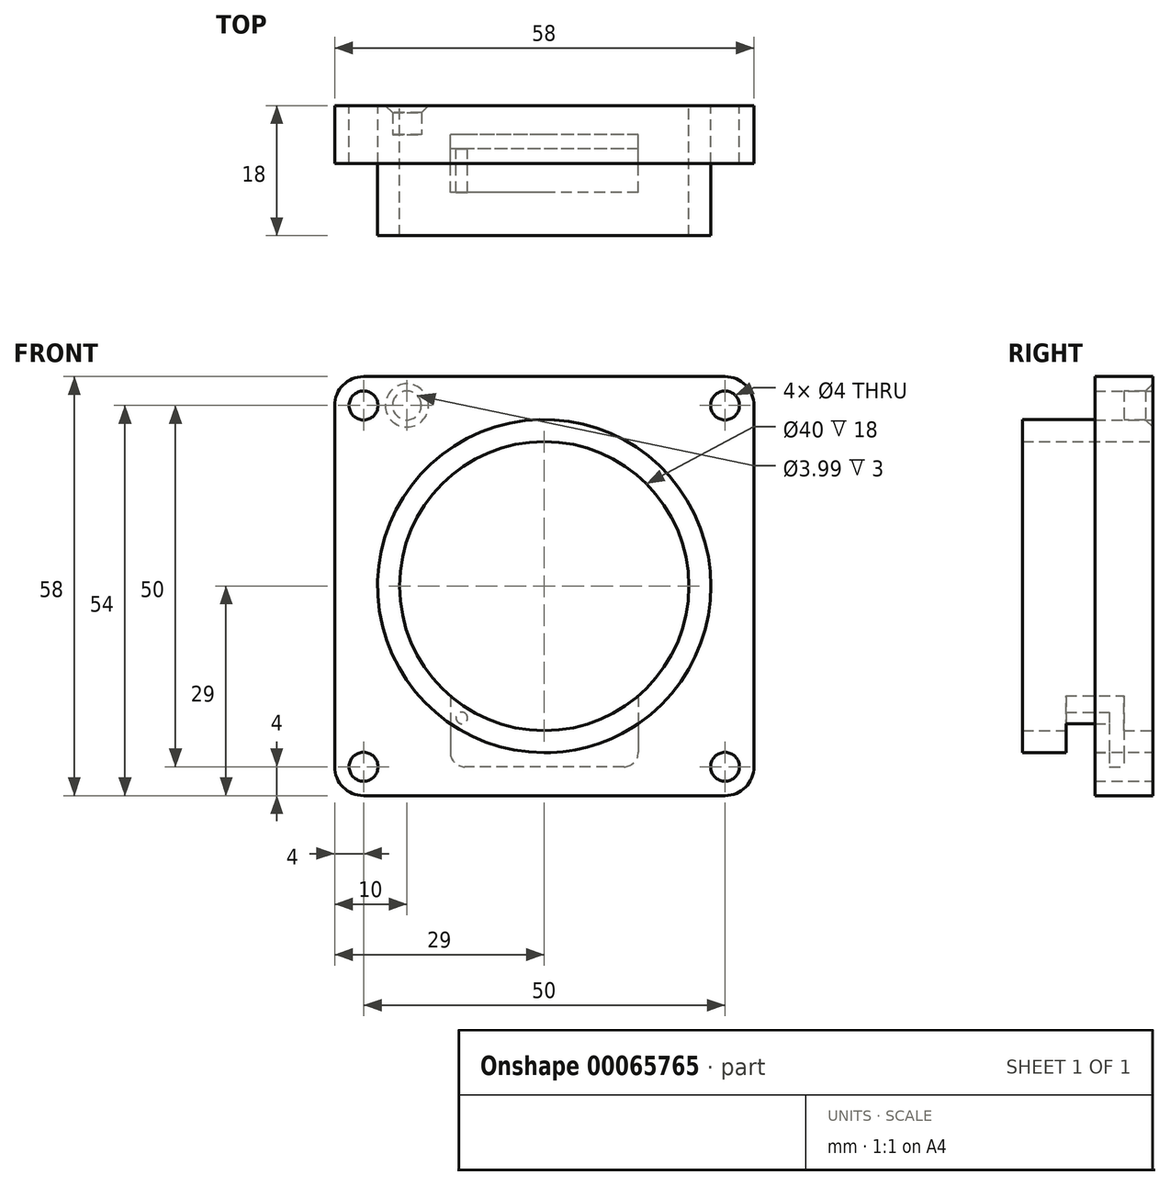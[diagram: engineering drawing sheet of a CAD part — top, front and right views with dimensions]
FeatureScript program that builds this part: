
annotation { "Feature Type Name" : "Feature", "Feature Type Description" : "" }
export const myFeature = defineFeature(function(context is Context, id is Id, definition is map)
    precondition{}
    {
        {
            var Q0;
            Q0=qCreatedBy(makeId("Front.planeOp"),FACE);
            var sketch = newSketch(context, id + "F0", { "sketchPlane" : qUnion([Q0])});
            skLineSegment(sketch, "E0.bottom", {"start": v(25, 29) * mm, "end": v(-25, 29) * mm});
            skLineSegment(sketch, "E0.top", {"start": v(25, -29) * mm, "end": v(-25, -29) * mm});
            skLineSegment(sketch, "E0.left", {"start": v(29, 25) * mm, "end": v(29, -25) * mm});
            skLineSegment(sketch, "E0.right", {"start": v(-29, 25) * mm, "end": v(-29, -25) * mm});
            skPoint(sketch, "E1", {"position": v(0, 29) * mm});
            skPoint(sketch, "E2", {"position": v(29, 0) * mm});
            skCircle(sketch, "E3", {"center": v(-25, 25) * mm, "radius": 2 * mm});
            skCircle(sketch, "E4.MirrorC", {"center": v(25, 25) * mm, "radius": 2 * mm});
            skCircle(sketch, "E5.MirrorC", {"center": v(-25, -25) * mm, "radius": 2 * mm});
            skCircle(sketch, "E6.MirrorC", {"center": v(25, -25) * mm, "radius": 2 * mm});
            skPoint(sketch, "E7.visualSharp", {"position": v(-29, 29) * mm});
            skArc(sketch, "E7.filletArc", {"start": v(-25, 29) * mm, "mid": v(-27.83, 27.83) * mm, "end": v(-29, 25) * mm});
            skPoint(sketch, "E8.visualSharp", {"position": v(29, 29) * mm});
            skArc(sketch, "E8.filletArc", {"start": v(29, 25) * mm, "mid": v(27.83, 27.83) * mm, "end": v(25, 29) * mm});
            skPoint(sketch, "E9.visualSharp", {"position": v(29, -29) * mm});
            skArc(sketch, "E9.filletArc", {"start": v(25, -29) * mm, "mid": v(27.83, -27.83) * mm, "end": v(29, -25) * mm});
            skPoint(sketch, "E10.visualSharp", {"position": v(-29, -29) * mm});
            skArc(sketch, "E10.filletArc", {"start": v(-29, -25) * mm, "mid": v(-27.83, -27.83) * mm, "end": v(-25, -29) * mm});
            skCircle(sketch, "E11", {"center": v(0, 0) * mm, "radius": 20 * mm});
            skSolve(sketch);
        }
        {
            var Q0;
            Q0=makeQuery(id+"F0.imprint","IMPRINT",FACE,{"disambiguationData":[TD([[makeQuery(id+"F0.imprint","IMPRINT",EDGE,{"derivedFrom":sQuery(id+"F0.wireOp",EDGE,"E0.bottom")}),1.0]])]});
            extrude(context, id + "F1", {"entities" : qUnion([Q0]), "depth" : 4 * mm});
        }
        {
            var Q0;
            Q0=makeQuery(id+"F1.opExtrude","CAP_FACE",FACE,{"disambiguationData":[OSD([sQuery(id+"F0.wireOp",EDGE,"E0.bottom"),sQuery(id+"F0.wireOp",EDGE,"E0.top"),sQuery(id+"F0.wireOp",EDGE,"E0.left"),sQuery(id+"F0.wireOp",EDGE,"E0.right"),sQuery(id+"F0.wireOp",EDGE,"E3"),sQuery(id+"F0.wireOp",EDGE,"E4.MirrorC"),sQuery(id+"F0.wireOp",EDGE,"E5.MirrorC"),sQuery(id+"F0.wireOp",EDGE,"E6.MirrorC"),sQuery(id+"F0.wireOp",EDGE,"E7.filletArc"),sQuery(id+"F0.wireOp",EDGE,"E8.filletArc"),sQuery(id+"F0.wireOp",EDGE,"E9.filletArc"),sQuery(id+"F0.wireOp",EDGE,"E10.filletArc"),sQuery(id+"F0.wireOp",EDGE,"74017124-3e05-427a-b8e4-af609694847d.bottom"),sQuery(id+"F0.wireOp",EDGE,"74017124-3e05-427a-b8e4-af609694847d.top"),sQuery(id+"F0.wireOp",EDGE,"74017124-3e05-427a-b8e4-af609694847d.left"),sQuery(id+"F0.wireOp",EDGE,"74017124-3e05-427a-b8e4-af609694847d.right"),sQuery(id+"F0.wireOp",EDGE,"8a5725f9-208e-47c7-ad8a-a344d27b9ad4.filletArc"),sQuery(id+"F0.wireOp",EDGE,"34e853ff-a61b-4a46-9221-9543787036cd.filletArc"),sQuery(id+"F0.wireOp",EDGE,"1b7ca9ec-e36b-44de-8ecb-2f01a231179c.filletArc"),sQuery(id+"F0.wireOp",EDGE,"5f012eeb-bb5c-4c35-9c7e-adf75f7540f9.filletArc")])],"isStart":true});
            var sketch = newSketch(context, id + "F2", { "sketchPlane" : qUnion([Q0])});
            skCircle(sketch, "E12", {"center": v(-19, 25) * mm, "radius": 2 * mm});
            skLineSegment(sketch, "E13", {"start": v(-25, 25) * mm, "end": v(25, 25) * mm, "construction": true});
            skLineSegment(sketch, "E14", {"start": v(25, 25) * mm, "end": v(25, -25) * mm, "construction": true});
            skLineSegment(sketch, "E15", {"start": v(25, -25) * mm, "end": v(-25, -25) * mm, "construction": true});
            skLineSegment(sketch, "E16", {"start": v(-25, -25) * mm, "end": v(-25, 25) * mm, "construction": true});
            skCircle(sketch, "E17.MirrorC", {"center": v(19, 25) * mm, "radius": 2 * mm});
            skCircle(sketch, "E18.MirrorC", {"center": v(19, -25) * mm, "radius": 2 * mm});
            skCircle(sketch, "E19", {"center": v(-16, -25) * mm, "radius": 2 * mm});
            skSolve(sketch);
        }
        {
            var Q0;
            Q0=makeQuery(id+"F2.imprint","IMPRINT",FACE,{"disambiguationData":[TD([[makeQuery(id+"F2.imprint","IMPRINT",EDGE,{"derivedFrom":sQuery(id+"F2.wireOp",EDGE,"E12")}),1.0]])]});
            var Q1;
            Q1=makeQuery(id+"F2.imprint","IMPRINT",FACE,{"disambiguationData":[TD([[makeQuery(id+"F2.imprint","IMPRINT",EDGE,{"derivedFrom":sQuery(id+"F2.wireOp",EDGE,"E17.MirrorC")}),-1.0]])]});
            var Q2;
            Q2=makeQuery(id+"F2.imprint","IMPRINT",FACE,{"disambiguationData":[TD([[makeQuery(id+"F2.imprint","IMPRINT",EDGE,{"derivedFrom":sQuery(id+"F2.wireOp",EDGE,"E18.MirrorC")}),1.0]])]});
            var Q3;
            Q3=makeQuery(id+"F2.imprint","IMPRINT",FACE,{"disambiguationData":[TD([[makeQuery(id+"F2.imprint","IMPRINT",EDGE,{"derivedFrom":sQuery(id+"F2.wireOp",EDGE,"E19")}),1.0]])]});
            extrude(context, id + "F3", {"entities" : qUnion([Q0, Q1, Q2, Q3]), "operationType" : NewBodyOperationType.ADD, "depth" : 4 * mm});
        }
        {
            var Q0;
            Q0=makeQuery(id+"F3.opExtrude","CAP_EDGE",EDGE,{"disambiguationData":[OSD([sQuery(id+"F2.wireOp",EDGE,"E19")])],"isStart":false});
            var Q1;
            Q1=makeQuery(id+"F3.opExtrude","CAP_EDGE",EDGE,{"disambiguationData":[OSD([sQuery(id+"F2.wireOp",EDGE,"E18.MirrorC")])],"isStart":false});
            var Q2;
            Q2=makeQuery(id+"F3.opExtrude","CAP_EDGE",EDGE,{"disambiguationData":[OSD([sQuery(id+"F2.wireOp",EDGE,"E17.MirrorC")])],"isStart":false});
            var Q3;
            Q3=makeQuery(id+"F3.opExtrude","CAP_EDGE",EDGE,{"disambiguationData":[OSD([sQuery(id+"F2.wireOp",EDGE,"E12")])],"isStart":false});
            chamfer(context, id + "F4", {"entities" : qUnion([Q0, Q1, Q2, Q3]), "width" : 1 * mm, "tangentPropagation" : true});
        }
        {
            var Q0;
            Q0=makeQuery(id+"F1.opExtrude","CAP_FACE",FACE,{"disambiguationData":[OSD([sQuery(id+"F0.wireOp",EDGE,"E0.bottom"),sQuery(id+"F0.wireOp",EDGE,"E0.top"),sQuery(id+"F0.wireOp",EDGE,"E0.left"),sQuery(id+"F0.wireOp",EDGE,"E0.right"),sQuery(id+"F0.wireOp",EDGE,"E3"),sQuery(id+"F0.wireOp",EDGE,"E4.MirrorC"),sQuery(id+"F0.wireOp",EDGE,"E5.MirrorC"),sQuery(id+"F0.wireOp",EDGE,"E6.MirrorC"),sQuery(id+"F0.wireOp",EDGE,"E7.filletArc"),sQuery(id+"F0.wireOp",EDGE,"E8.filletArc"),sQuery(id+"F0.wireOp",EDGE,"E9.filletArc"),sQuery(id+"F0.wireOp",EDGE,"E10.filletArc"),sQuery(id+"F0.wireOp",EDGE,"74017124-3e05-427a-b8e4-af609694847d.bottom"),sQuery(id+"F0.wireOp",EDGE,"74017124-3e05-427a-b8e4-af609694847d.top"),sQuery(id+"F0.wireOp",EDGE,"74017124-3e05-427a-b8e4-af609694847d.left"),sQuery(id+"F0.wireOp",EDGE,"74017124-3e05-427a-b8e4-af609694847d.right"),sQuery(id+"F0.wireOp",EDGE,"8a5725f9-208e-47c7-ad8a-a344d27b9ad4.filletArc"),sQuery(id+"F0.wireOp",EDGE,"34e853ff-a61b-4a46-9221-9543787036cd.filletArc"),sQuery(id+"F0.wireOp",EDGE,"1b7ca9ec-e36b-44de-8ecb-2f01a231179c.filletArc"),sQuery(id+"F0.wireOp",EDGE,"5f012eeb-bb5c-4c35-9c7e-adf75f7540f9.filletArc")])],"isStart":false});
            var sketch = newSketch(context, id + "F5", { "sketchPlane" : qUnion([Q0])});
            skCircle(sketch, "E20", {"center": v(0, 0) * mm, "radius": 23.05 * mm});
            skCircle(sketch, "E21", {"center": v(0, 0) * mm, "radius": 20 * mm});
            skSolve(sketch);
        }
        {
            var Q0;
            Q0=makeQuery(id+"F5.imprint","IMPRINT",FACE,{"disambiguationData":[TD([[makeQuery(id+"F5.imprint","IMPRINT",EDGE,{"derivedFrom":sQuery(id+"F5.wireOp",EDGE,"E20")}),1.0]])]});
            extrude(context, id + "F6", {"entities" : qUnion([Q0]), "operationType" : NewBodyOperationType.ADD, "depth" : 10 * mm});
        }
        {
            var Q0;
            Q0=makeQuery(id+"F1.opExtrude","CAP_FACE",FACE,{"disambiguationData":[OSD([sQuery(id+"F0.wireOp",EDGE,"E0.bottom"),sQuery(id+"F0.wireOp",EDGE,"E0.top"),sQuery(id+"F0.wireOp",EDGE,"E0.left"),sQuery(id+"F0.wireOp",EDGE,"E0.right"),sQuery(id+"F0.wireOp",EDGE,"E3"),sQuery(id+"F0.wireOp",EDGE,"E4.MirrorC"),sQuery(id+"F0.wireOp",EDGE,"E5.MirrorC"),sQuery(id+"F0.wireOp",EDGE,"E6.MirrorC"),sQuery(id+"F0.wireOp",EDGE,"E7.filletArc"),sQuery(id+"F0.wireOp",EDGE,"E8.filletArc"),sQuery(id+"F0.wireOp",EDGE,"E9.filletArc"),sQuery(id+"F0.wireOp",EDGE,"E10.filletArc"),sQuery(id+"F0.wireOp",EDGE,"E11")])],"isStart":true});
            var sketch = newSketch(context, id + "F7", { "sketchPlane" : qUnion([Q0])});
            skLineSegment(sketch, "E22.bottom", {"start": v(-13, -10) * mm, "end": v(13, -10) * mm});
            skLineSegment(sketch, "E22.top", {"start": v(-11, -25) * mm, "end": v(11, -25) * mm});
            skLineSegment(sketch, "E22.left", {"start": v(-13, -10) * mm, "end": v(-13, -23) * mm});
            skLineSegment(sketch, "E22.right", {"start": v(13, -10) * mm, "end": v(13, -23) * mm});
            skArc(sketch, "E23.0.0", {"start": v(-25, 29) * mm, "mid": v(-27.83, 27.83) * mm, "end": v(-29, 25) * mm});
            skLineSegment(sketch, "E23.0.1", {"start": v(-29, 25) * mm, "end": v(-29, -25) * mm});
            skArc(sketch, "E23.0.2", {"start": v(-29, -25) * mm, "mid": v(-27.83, -27.83) * mm, "end": v(-25, -29) * mm});
            skLineSegment(sketch, "E23.0.3", {"start": v(-25, -29) * mm, "end": v(25, -29) * mm});
            skArc(sketch, "E23.0.4", {"start": v(25, -29) * mm, "mid": v(27.83, -27.83) * mm, "end": v(29, -25) * mm});
            skLineSegment(sketch, "E23.0.5", {"start": v(29, -25) * mm, "end": v(29, 25) * mm});
            skArc(sketch, "E23.0.6", {"start": v(29, 25) * mm, "mid": v(27.83, 27.83) * mm, "end": v(25, 29) * mm});
            skLineSegment(sketch, "E23.0.7", {"start": v(25, 29) * mm, "end": v(-25, 29) * mm});
            skLineSegment(sketch, "E24", {"start": v(-25, -25) * mm, "end": v(25, -25) * mm, "construction": true});
            skPoint(sketch, "E25", {"position": v(0, -10) * mm});
            skPoint(sketch, "E26.visualSharp", {"position": v(-13, -25) * mm});
            skArc(sketch, "E26.filletArc", {"start": v(-13, -23) * mm, "mid": v(-12.41, -24.41) * mm, "end": v(-11, -25) * mm});
            skPoint(sketch, "E27.visualSharp", {"position": v(13, -25) * mm});
            skArc(sketch, "E27.filletArc", {"start": v(11, -25) * mm, "mid": v(12.41, -24.41) * mm, "end": v(13, -23) * mm});
            skSolve(sketch);
        }
        {
            var Q0;
            {var subQ0=sQuery(id+"F7.wireOp",EDGE,"E22.top");Q0=makeQuery(id+"F7.imprint","IMPRINT",FACE,{"disambiguationData":[TD([[makeQuery(id+"F7.imprint","IMPRINT",EDGE,{"derivedFrom":subQ0}),1.0]])]});}
            extrude(context, id + "F8", {"entities" : qUnion([Q0]), "operationType" : NewBodyOperationType.REMOVE, "oppositeDirection" : true, "depth" : 2 * mm});
        }
        {
            var Q0;
            Q0=makeQuery(id+"F8.boolean.opBoolean","COPY",FACE,{"derivedFrom":makeQuery(id+"F8.opExtrude","CAP_FACE",FACE,{"disambiguationData":[OSD([sQuery(id+"F0.wireOp",EDGE,"E11"),sQuery(id+"F7.wireOp",EDGE,"E22.top"),sQuery(id+"F7.wireOp",EDGE,"E22.left"),sQuery(id+"F7.wireOp",EDGE,"E22.right"),sQuery(id+"F7.wireOp",EDGE,"E26.filletArc"),sQuery(id+"F7.wireOp",EDGE,"E27.filletArc")])],"isStart":false})});
            var sketch = newSketch(context, id + "F9", { "sketchPlane" : qUnion([Q0])});
            skCircle(sketch, "E28", {"center": v(-11.4, -18.25) * mm, "radius": 0.8 * mm});
            skCircle(sketch, "E29.0.0", {"center": v(0, 0) * mm, "radius": 23.05 * mm});
            skLineSegment(sketch, "E30", {"start": v(-10.6, -16.96) * mm, "end": v(-12.21, -19.55) * mm, "construction": true});
            skCircle(sketch, "E31.MirrorC", {"center": v(11.4, -18.25) * mm, "radius": 0.8 * mm});
            skSolve(sketch);
        }
        {
            var Q0;
            Q0=makeQuery(id+"F9.imprint","IMPRINT",FACE,{"disambiguationData":[TD([[makeQuery(id+"F9.imprint","IMPRINT",EDGE,{"derivedFrom":sQuery(id+"F9.wireOp",EDGE,"E28")}),1.0]])]});
            var Q1;
            Q1=makeQuery(id+"F9.imprint","IMPRINT",FACE,{"disambiguationData":[TD([[makeQuery(id+"F9.imprint","IMPRINT",EDGE,{"derivedFrom":sQuery(id+"F9.wireOp",EDGE,"E31.MirrorC")}),-1.0]])]});
            extrude(context, id + "F10", {"entities" : qUnion([Q0, Q1]), "operationType" : NewBodyOperationType.REMOVE, "oppositeDirection" : true, "depth" : 6 * mm});
        }
    });
